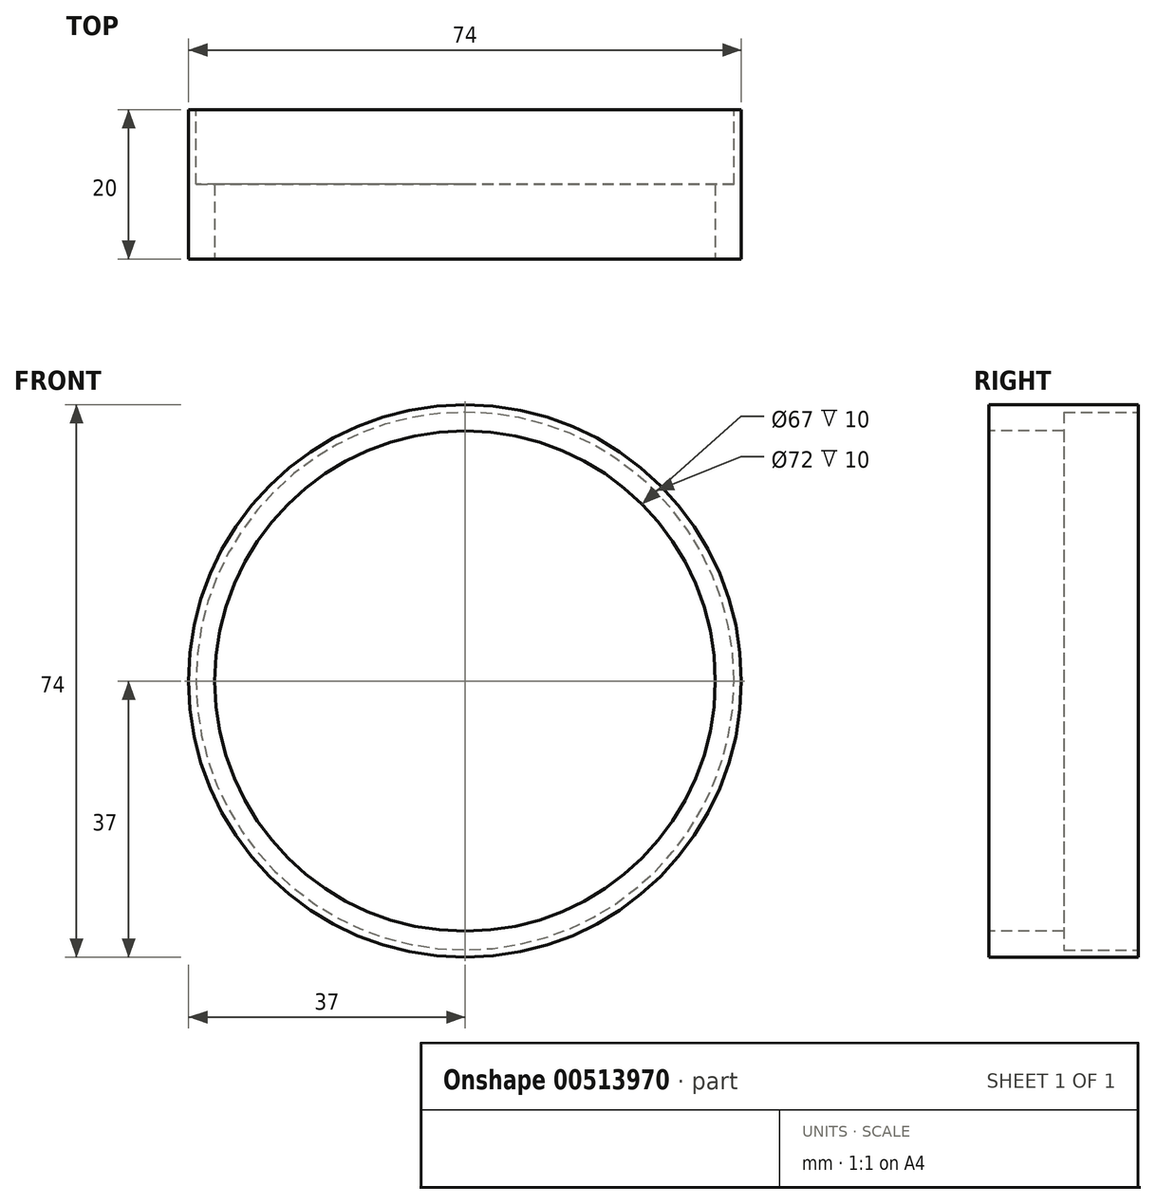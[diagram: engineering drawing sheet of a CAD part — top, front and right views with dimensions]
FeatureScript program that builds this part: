
annotation { "Feature Type Name" : "Feature", "Feature Type Description" : "" }
export const myFeature = defineFeature(function(context is Context, id is Id, definition is map)
    precondition{}
    {
        {
            var Q0;
            Q0=qCreatedBy(makeId("Front.planeOp"),FACE);
            var sketch = newSketch(context, id + "F0", { "sketchPlane" : qUnion([Q0])});
            skCircle(sketch, "E0", {"center": v(0, 0) * mm, "radius": 37 * mm});
            skSolve(sketch);
        }
        {
            var Q0;
            Q0=makeQuery(id+"F0.imprint","IMPRINT",FACE,{"disambiguationData":[TD([[makeQuery(id+"F0.imprint","IMPRINT",EDGE,{"derivedFrom":sQuery(id+"F0.wireOp",EDGE,"E0")}),1.0]])]});
            extrude(context, id + "F1", {"entities" : qUnion([Q0]), "depth" : 20 * mm});
        }
        {
            var Q0;
            Q0=makeQuery(id+"F1.opExtrude","CAP_FACE",FACE,{"disambiguationData":[OSD([sQuery(id+"F0.wireOp",EDGE,"E0")])],"isStart":false});
            var sketch = newSketch(context, id + "F2", { "sketchPlane" : qUnion([Q0])});
            skCircle(sketch, "E1", {"center": v(0, 0) * mm, "radius": 33.5 * mm});
            skSolve(sketch);
        }
        {
            var Q0;
            Q0 = qSketchRegion(id + "F2", true);
            extrude(context, id + "F3", {"entities" : qUnion([Q0]), "operationType" : NewBodyOperationType.REMOVE, "oppositeDirection" : true, "depth" : 25 * mm});
        }
        {
            var Q0;
            Q0=makeQuery(id+"F1.opExtrude","CAP_FACE",FACE,{"disambiguationData":[OSD([sQuery(id+"F0.wireOp",EDGE,"E0")])],"isStart":true});
            var sketch = newSketch(context, id + "F4", { "sketchPlane" : qUnion([Q0])});
            skCircle(sketch, "E2", {"center": v(0, 0) * mm, "radius": 36 * mm});
            skSolve(sketch);
        }
        {
            var Q0;
            Q0 = qSketchRegion(id + "F4", true);
            extrude(context, id + "F5", {"entities" : qUnion([Q0]), "operationType" : NewBodyOperationType.REMOVE, "oppositeDirection" : true, "depth" : 10 * mm});
        }
    });
